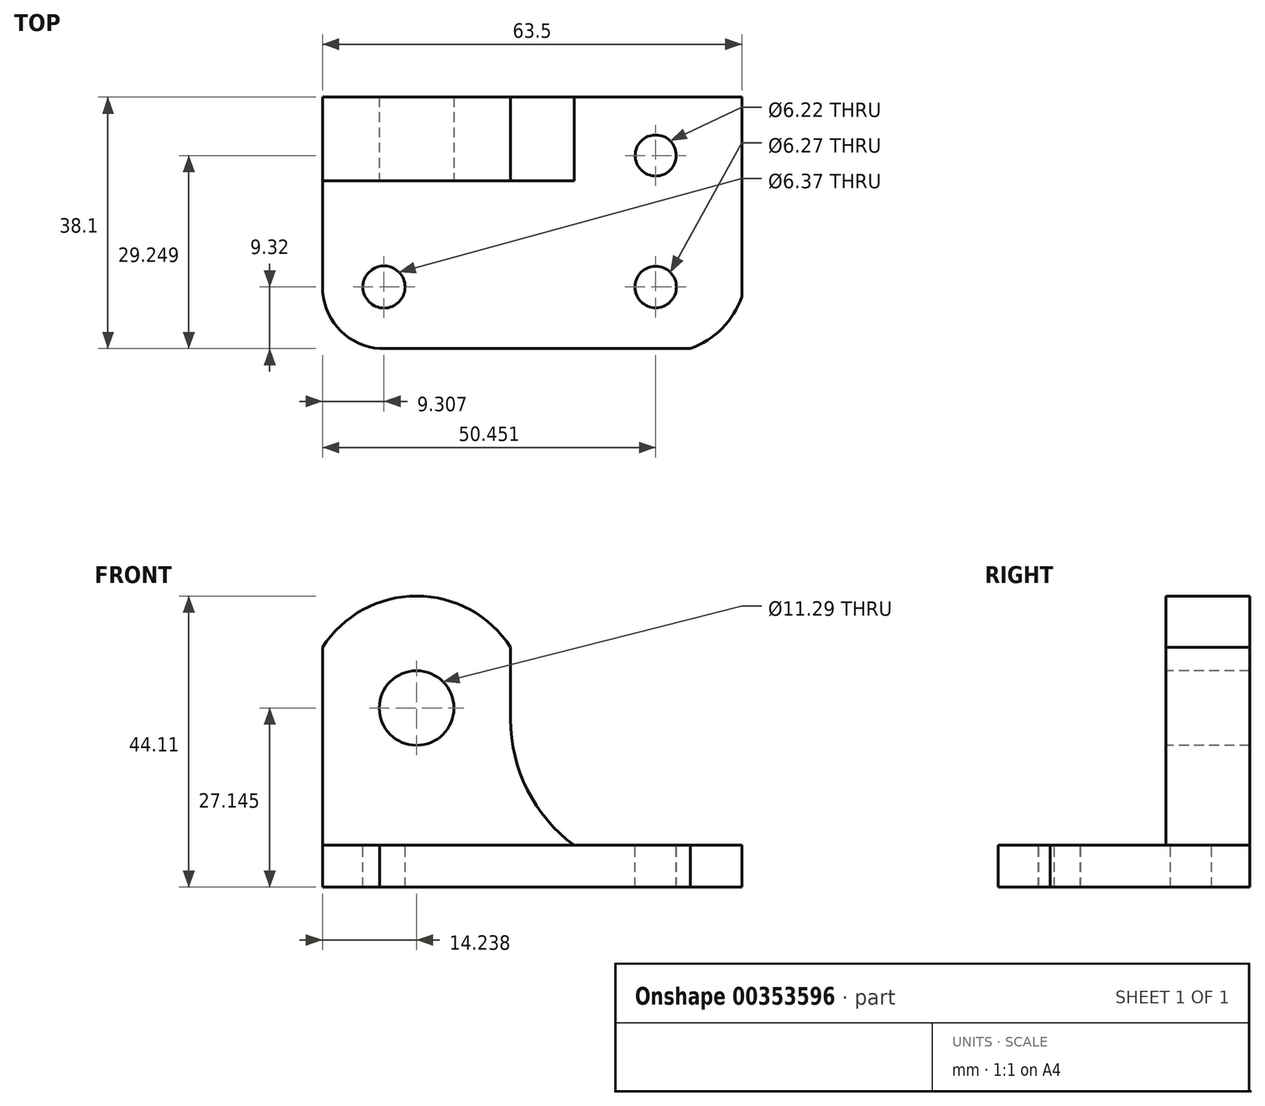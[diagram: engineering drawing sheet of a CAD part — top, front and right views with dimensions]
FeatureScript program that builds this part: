
annotation { "Feature Type Name" : "Feature", "Feature Type Description" : "" }
export const myFeature = defineFeature(function(context is Context, id is Id, definition is map)
    precondition{}
    {
        {
            var Q0;
            Q0=qCreatedBy(makeId("Top.planeOp"),FACE);
            var sketch = newSketch(context, id + "F0", { "sketchPlane" : qUnion([Q0])});
            skLineSegment(sketch, "E0.bottom", {"start": v(0, 0) * mm, "end": v(63.5, 0) * mm});
            skLineSegment(sketch, "E0.top", {"start": v(0, 38.1) * mm, "end": v(63.5, 38.1) * mm});
            skLineSegment(sketch, "E0.left", {"start": v(0, 0) * mm, "end": v(0, 38.1) * mm});
            skLineSegment(sketch, "E0.right", {"start": v(63.5, 0) * mm, "end": v(63.5, 38.1) * mm});
            skSolve(sketch);
        }
        {
            var Q0;
            Q0=makeQuery(id+"F0.imprint","IMPRINT",FACE,{"disambiguationData":[TD([[makeQuery(id+"F0.imprint","IMPRINT",EDGE,{"derivedFrom":sQuery(id+"F0.wireOp",EDGE,"E0.bottom")}),1.0]])]});
            extrude(context, id + "F1", {"entities" : qUnion([Q0]), "depth" : 6.35 * mm});
        }
        {
            var Q0;
            Q0=makeQuery(id+"F1.opExtrude","CAP_FACE",FACE,{"disambiguationData":[OSD([sQuery(id+"F0.wireOp",EDGE,"E0.bottom"),sQuery(id+"F0.wireOp",EDGE,"E0.top"),sQuery(id+"F0.wireOp",EDGE,"E0.left"),sQuery(id+"F0.wireOp",EDGE,"E0.right")])],"isStart":false});
            var sketch = newSketch(context, id + "F2", { "sketchPlane" : qUnion([Q0])});
            skArc(sketch, "E1", {"start": v(0, 8.51) * mm, "mid": v(2.76, 2.66) * mm, "end": v(8.67, 0) * mm});
            skArc(sketch, "E2", {"start": v(55.71, 0) * mm, "mid": v(60.5, 3.06) * mm, "end": v(63.5, 7.9) * mm});
            skSolve(sketch);
        }
        {
            var Q0;
            {var subQ0=sQuery(id+"F2.wireOp",EDGE,"E1");Q0=makeQuery(id+"F2.imprint","IMPRINT",FACE,{"disambiguationData":[TD([[makeQuery(id+"F2.imprint","IMPRINT",EDGE,{"derivedFrom":subQ0}),-1.0]])]});}
            var Q1;
            {var subQ0=sQuery(id+"F2.wireOp",EDGE,"E2");Q1=makeQuery(id+"F2.imprint","IMPRINT",FACE,{"disambiguationData":[TD([[makeQuery(id+"F2.imprint","IMPRINT",EDGE,{"derivedFrom":subQ0}),-1.0]])]});}
            extrude(context, id + "F3", {"entities" : qUnion([Q0, Q1]), "operationType" : NewBodyOperationType.REMOVE, "oppositeDirection" : true, "depth" : 25.4 * mm});
        }
        {
            var Q0;
            Q0=makeQuery(id+"F1.opExtrude","CAP_FACE",FACE,{"disambiguationData":[OSD([sQuery(id+"F0.wireOp",EDGE,"E0.bottom"),sQuery(id+"F0.wireOp",EDGE,"E0.top"),sQuery(id+"F0.wireOp",EDGE,"E0.left"),sQuery(id+"F0.wireOp",EDGE,"E0.right")])],"isStart":false});
            var sketch = newSketch(context, id + "F4", { "sketchPlane" : qUnion([Q0])});
            skLineSegment(sketch, "E3.bottom", {"start": v(0, 38.1) * mm, "end": v(38.1, 38.1) * mm});
            skLineSegment(sketch, "E3.top", {"start": v(0, 25.4) * mm, "end": v(38.1, 25.4) * mm});
            skLineSegment(sketch, "E3.left", {"start": v(0, 38.1) * mm, "end": v(0, 25.4) * mm});
            skLineSegment(sketch, "E3.right", {"start": v(38.1, 38.1) * mm, "end": v(38.1, 25.4) * mm});
            skSolve(sketch);
        }
        {
            var Q0;
            Q0=makeQuery(id+"F4.imprint","IMPRINT",FACE,{"disambiguationData":[TD([[makeQuery(id+"F4.imprint","IMPRINT",EDGE,{"derivedFrom":sQuery(id+"F4.wireOp",EDGE,"E3.bottom")}),-1.0]])]});
            extrude(context, id + "F5", {"entities" : qUnion([Q0]), "operationType" : NewBodyOperationType.ADD, "depth" : 38.1 * mm});
        }
        {
            var Q0;
            Q0=makeQuery(id+"F5.opExtrude","SWEPT_FACE",FACE,{"disambiguationData":[OSD([sQuery(id+"F4.wireOp",EDGE,"E3.top")])]});
            var sketch = newSketch(context, id + "F6", { "sketchPlane" : qUnion([Q0])});
            skLineSegment(sketch, "E4", {"start": v(0, 36.37) * mm, "end": v(0, 44.45) * mm});
            skLineSegment(sketch, "E5", {"start": v(0, 44.45) * mm, "end": v(38.1, 44.45) * mm});
            skLineSegment(sketch, "E6", {"start": v(38.1, 44.45) * mm, "end": v(38.1, 25.4) * mm});
            skArc(sketch, "E7", {"start": v(28.48, 36.37) * mm, "mid": v(14.24, 44.1) * mm, "end": v(0, 36.37) * mm});
            skLineSegment(sketch, "E8", {"start": v(28.48, 36.37) * mm, "end": v(28.48, 25.4) * mm});
            skArc(sketch, "E9", {"start": v(28.48, 25.4) * mm, "mid": v(31.02, 14.73) * mm, "end": v(38.1, 6.35) * mm});
            skSolve(sketch);
        }
        {
            var Q0;
            Q0=makeQuery(id+"F6.imprint","IMPRINT",FACE,{"disambiguationData":[TD([[makeQuery(id+"F6.imprint","IMPRINT",EDGE,{"derivedFrom":sQuery(id+"F6.wireOp",EDGE,"E4")}),1.0]])]});
            extrude(context, id + "F7", {"entities" : qUnion([Q0]), "operationType" : NewBodyOperationType.REMOVE, "oppositeDirection" : true, "depth" : 25.4 * mm});
        }
        {
            var Q0;
            Q0=makeQuery(id+"F5.opExtrude","SWEPT_FACE",FACE,{"disambiguationData":[OSD([sQuery(id+"F4.wireOp",EDGE,"E3.top")])]});
            var sketch = newSketch(context, id + "F8", { "sketchPlane" : qUnion([Q0])});
            skCircle(sketch, "E10", {"center": v(14.24, 27.14) * mm, "radius": 5.65 * mm});
            skSolve(sketch);
        }
        {
            var Q0;
            Q0=makeQuery(id+"F8.imprint","IMPRINT",FACE,{"disambiguationData":[TD([[makeQuery(id+"F8.imprint","IMPRINT",EDGE,{"derivedFrom":sQuery(id+"F8.wireOp",EDGE,"E10")}),1.0]])]});
            extrude(context, id + "F9", {"entities" : qUnion([Q0]), "operationType" : NewBodyOperationType.REMOVE, "oppositeDirection" : true, "depth" : 25.4 * mm});
        }
        {
            var Q0;
            Q0=makeQuery(id+"F1.opExtrude","CAP_FACE",FACE,{"disambiguationData":[OSD([sQuery(id+"F0.wireOp",EDGE,"E0.bottom"),sQuery(id+"F0.wireOp",EDGE,"E0.top"),sQuery(id+"F0.wireOp",EDGE,"E0.left"),sQuery(id+"F0.wireOp",EDGE,"E0.right")])],"isStart":false});
            var sketch = newSketch(context, id + "F10", { "sketchPlane" : qUnion([Q0])});
            skCircle(sketch, "E11", {"center": v(9.3, 9.32) * mm, "radius": 3.19 * mm});
            skCircle(sketch, "E12", {"center": v(50.45, 9.32) * mm, "radius": 3.14 * mm});
            skCircle(sketch, "E13", {"center": v(50.45, 29.25) * mm, "radius": 3.11 * mm});
            skSolve(sketch);
        }
        {
            var Q0;
            Q0=makeQuery(id+"F10.imprint","IMPRINT",FACE,{"disambiguationData":[TD([[makeQuery(id+"F10.imprint","IMPRINT",EDGE,{"derivedFrom":sQuery(id+"F10.wireOp",EDGE,"E11")}),1.0]])]});
            var Q1;
            Q1=makeQuery(id+"F10.imprint","IMPRINT",FACE,{"disambiguationData":[TD([[makeQuery(id+"F10.imprint","IMPRINT",EDGE,{"derivedFrom":sQuery(id+"F10.wireOp",EDGE,"E12")}),1.0]])]});
            var Q2;
            Q2=makeQuery(id+"F10.imprint","IMPRINT",FACE,{"disambiguationData":[TD([[makeQuery(id+"F10.imprint","IMPRINT",EDGE,{"derivedFrom":sQuery(id+"F10.wireOp",EDGE,"E13")}),1.0]])]});
            extrude(context, id + "F11", {"entities" : qUnion([Q0, Q1, Q2]), "operationType" : NewBodyOperationType.REMOVE, "oppositeDirection" : true, "depth" : 25.4 * mm});
        }
    });
